# Revit family: Bottle_Filling_Station_Versatile_Bi-Level -Elkay-EZSTL8WSVR_SK_LK
name_source: partatom
category: Plumbing Fixtures
units: mm (PartAtom-declared; Revit-internal decimal feet)

## family parameters
Always vertical = Yes
Cut with Voids When Loaded = No
Maintain Annotation Orientation = No
OmniClass Number = 23.45.05.00
OmniClass Title = Sanitary Equipment
Part Type = Normal
Room Calculation Point = No
Round Connector Dimension = Use Diameter
Shared = No
Work Plane-Based = No

## types (4) — shared parameters
Activation Method = Electronic Bottle Filler Sensor with Electronic Front and Side Bubbler Pushbar
Approx. Shipping Weight (lbs) = 103
CW Connection = No
Chilling Capacity(GPH) = 8
Current = 0 A
Electrical connection distance from floor level = 17.438 "
Inlet Connection Size (inch) = 0.375 "
Main Material = Finish-Elkay-Stainless Steel
Manufacturer = Elkay Manufacturer Company
Manufacturer Brand = Elkay (by Zurn Elkay Water Solutions)
Number of Poles = 1
Outlet Connection Size (inch) = 1.5 "
Power Factor = 1
Product Documentation Link = https://www.elkayfiles.com
Product Installation Sheet URL = https://www.elkayfiles.com
Product Page URL = https://www.elkay.com
Product Weight (lbs) = 84
Product data URL = https://bimobject.com
Repair Parts URL = https://www.elkayfiles.com
URL = https://www.elkay.com
Voltage = 115 V
Waste Connection = No
Waste line = 21.875 "
Water supply = 19 "
zero-valued in all types: Default Elevation

## per-type parameters (varying)
| type | Assembly Code | Bi-Level Water cooler | Description | Electrical connection | Model | Wrapper_Material |
| EZSTL8WSVRLK ( Right-Hand high side model) (Bottle Filling Station & Versatile Bi-Level ADA Cooler) | D2010810 | 0 " | ezH2O®  Bottle Filling Station & Versatile Bi-Level ADA Vandal Resistant Cooler Non-Filtered Refrigerated Light Gray | 0 " | EZSTL8WSVRLK | Finish-Elkay-Light Grey |
| EZSTL8WSVRLK  (Left-Hand high side model ) (Bottle Filling Station & Versatile Bi-Level ADA Cooler) | D2010800 | 36.75 " | ezH2O®  Bottle Filling Station & Versatile Bi-Level ADA Vandal Resistant Cooler Non-Filtered Refrigerated Light Gray | 6.625 " | EZSTL8WSVRLK | Finish-Elkay-Light Grey |
| EZSTL8WSVRSK (Right-Hand high side model)  (Bottle Filling Station & Versatile Bi-Level ADA Cooler) | D2010810 | 0 " | ezH2O®  Bottle Filling Station & Versatile Bi-Level ADA Vandal Resistant Cooler Non-Filtered Refrigerated Stainless | 6.625 " | EZSTL8WSVRSK | Finish-Elkay-Light Grey |
| EZSTL8WSVRSK (Left-Hand high side model)  (Bottle Filling Station & Versatile Bi-Level ADA Cooler) | D2010810 | 36.75 " | ezH2O®  Bottle Filling Station & Versatile Bi-Level ADA Vandal Resistant Cooler Non-Filtered Refrigerated Stainless | 6.625 " | EZSTL8WSVRSK | Finish-Elkay-Stainless Steel |

## geometry (parser evidence)
native form markers: Sweep x24
no freeform markers — native parametric forms only
